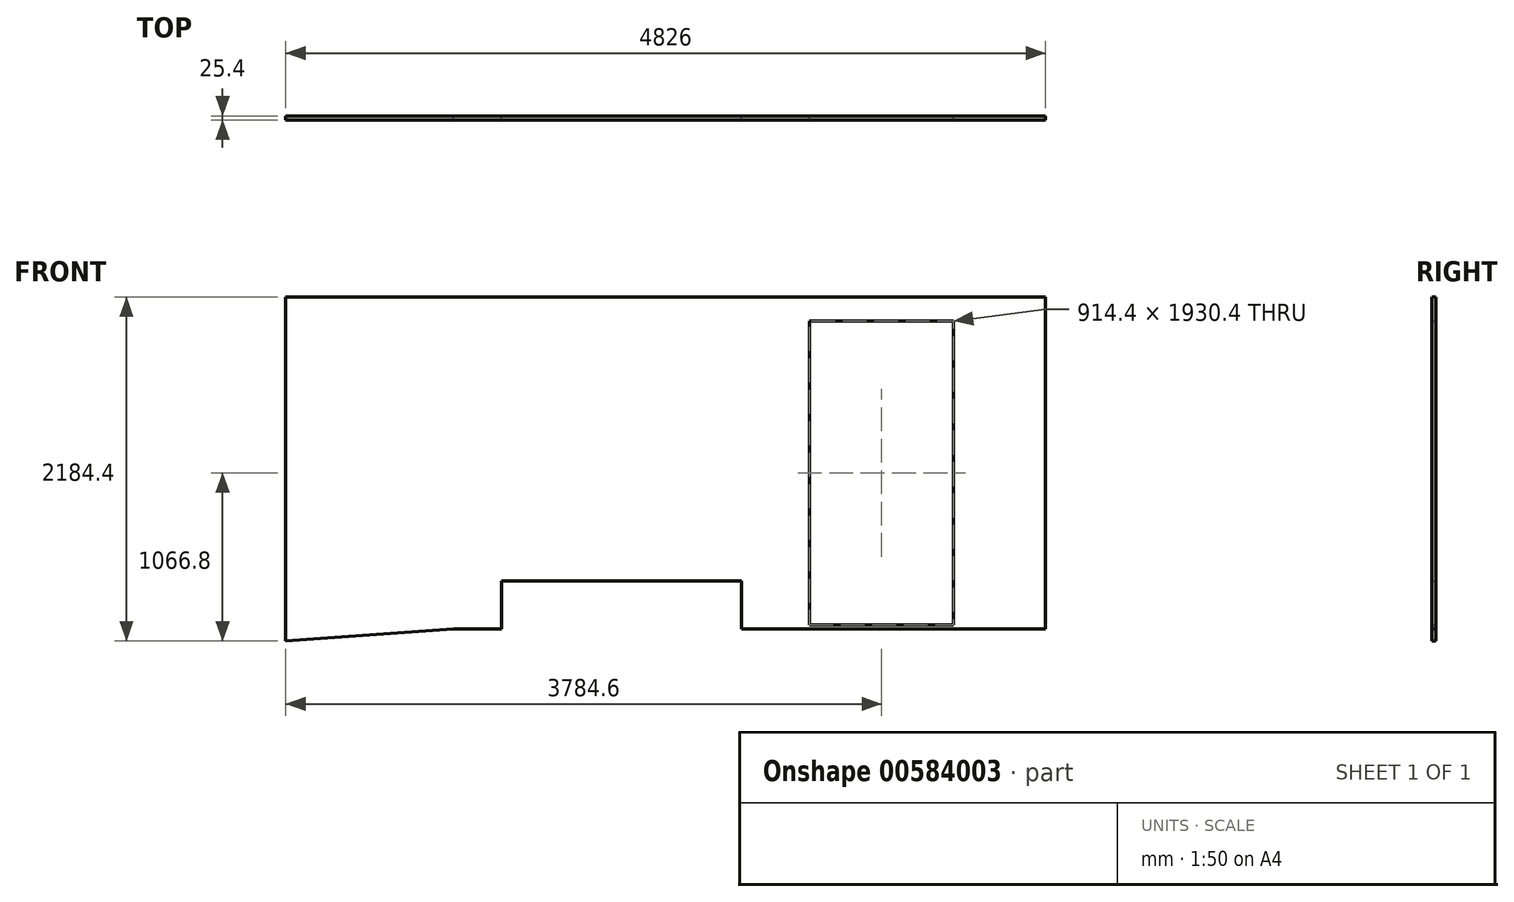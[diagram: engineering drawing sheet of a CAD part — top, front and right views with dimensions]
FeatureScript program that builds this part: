
annotation { "Feature Type Name" : "Feature", "Feature Type Description" : "" }
export const myFeature = defineFeature(function(context is Context, id is Id, definition is map)
    precondition{}
    {
        {
            var Q0;
            Q0=qCreatedBy(makeId("Front.planeOp"),FACE);
            var sketch = newSketch(context, id + "F0", { "sketchPlane" : qUnion([Q0])});
            skLineSegment(sketch, "E0", {"start": v(-1367.11, -857.03) * mm, "end": v(-1062.31, -857.03) * mm});
            skLineSegment(sketch, "E1", {"start": v(-1062.31, -552.23) * mm, "end": v(461.69, -552.23) * mm});
            skLineSegment(sketch, "E2", {"start": v(461.69, -552.23) * mm, "end": v(461.69, -857.03) * mm});
            skLineSegment(sketch, "E3", {"start": v(461.69, -857.03) * mm, "end": v(2392.09, -857.03) * mm});
            skLineSegment(sketch, "E4", {"start": v(2392.09, -857.03) * mm, "end": v(2392.09, 1251.17) * mm});
            skLineSegment(sketch, "E5", {"start": v(2392.09, 1251.17) * mm, "end": v(-2433.91, 1251.17) * mm});
            skLineSegment(sketch, "E6", {"start": v(-2433.91, 1251.17) * mm, "end": v(-2433.91, -933.23) * mm});
            skLineSegment(sketch, "E7", {"start": v(-1062.31, -552.23) * mm, "end": v(-1062.31, -857.03) * mm});
            skLineSegment(sketch, "E8", {"start": v(-1367.11, 1251.17) * mm, "end": v(-1367.11, -857.03) * mm, "construction": true});
            skPoint(sketch, "E9.orphan", {"position": v(-1367.11, 0) * mm});
            skLineSegment(sketch, "E10", {"start": v(-1367.11, -857.03) * mm, "end": v(-2433.91, -933.23) * mm});
            skLineSegment(sketch, "E11.bottom", {"start": v(1807.89, 1098.77) * mm, "end": v(893.49, 1098.77) * mm});
            skLineSegment(sketch, "E11.top", {"start": v(1807.89, -831.63) * mm, "end": v(893.49, -831.63) * mm});
            skLineSegment(sketch, "E11.left", {"start": v(1807.89, 1098.77) * mm, "end": v(1807.89, -831.63) * mm});
            skLineSegment(sketch, "E11.right", {"start": v(893.49, 1098.77) * mm, "end": v(893.49, -831.63) * mm});
            skLineSegment(sketch, "E12", {"start": v(893.49, -831.63) * mm, "end": v(461.69, -831.63) * mm, "construction": true});
            skLineSegment(sketch, "E13", {"start": v(1807.89, -831.63) * mm, "end": v(2392.09, -831.63) * mm, "construction": true});
            skLineSegment(sketch, "E14", {"start": v(-1062.31, -831.63) * mm, "end": v(-1367.11, -831.63) * mm, "construction": true});
            skLineSegment(sketch, "E15", {"start": v(-1367.11, -831.63) * mm, "end": v(-2433.91, -907.83) * mm, "construction": true});
            skSolve(sketch);
        }
        {
            var Q0;
            Q0=makeQuery(id+"F0.imprint","IMPRINT",FACE,{"disambiguationData":[TD([[makeQuery(id+"F0.imprint","IMPRINT",EDGE,{"derivedFrom":sQuery(id+"F0.wireOp",EDGE,"E0")}),1.0]])]});
            extrude(context, id + "F1", {"entities" : qUnion([Q0]), "depth" : 25.4 * mm, "offsetDistance" : 25.4 * mm});
        }
    });
